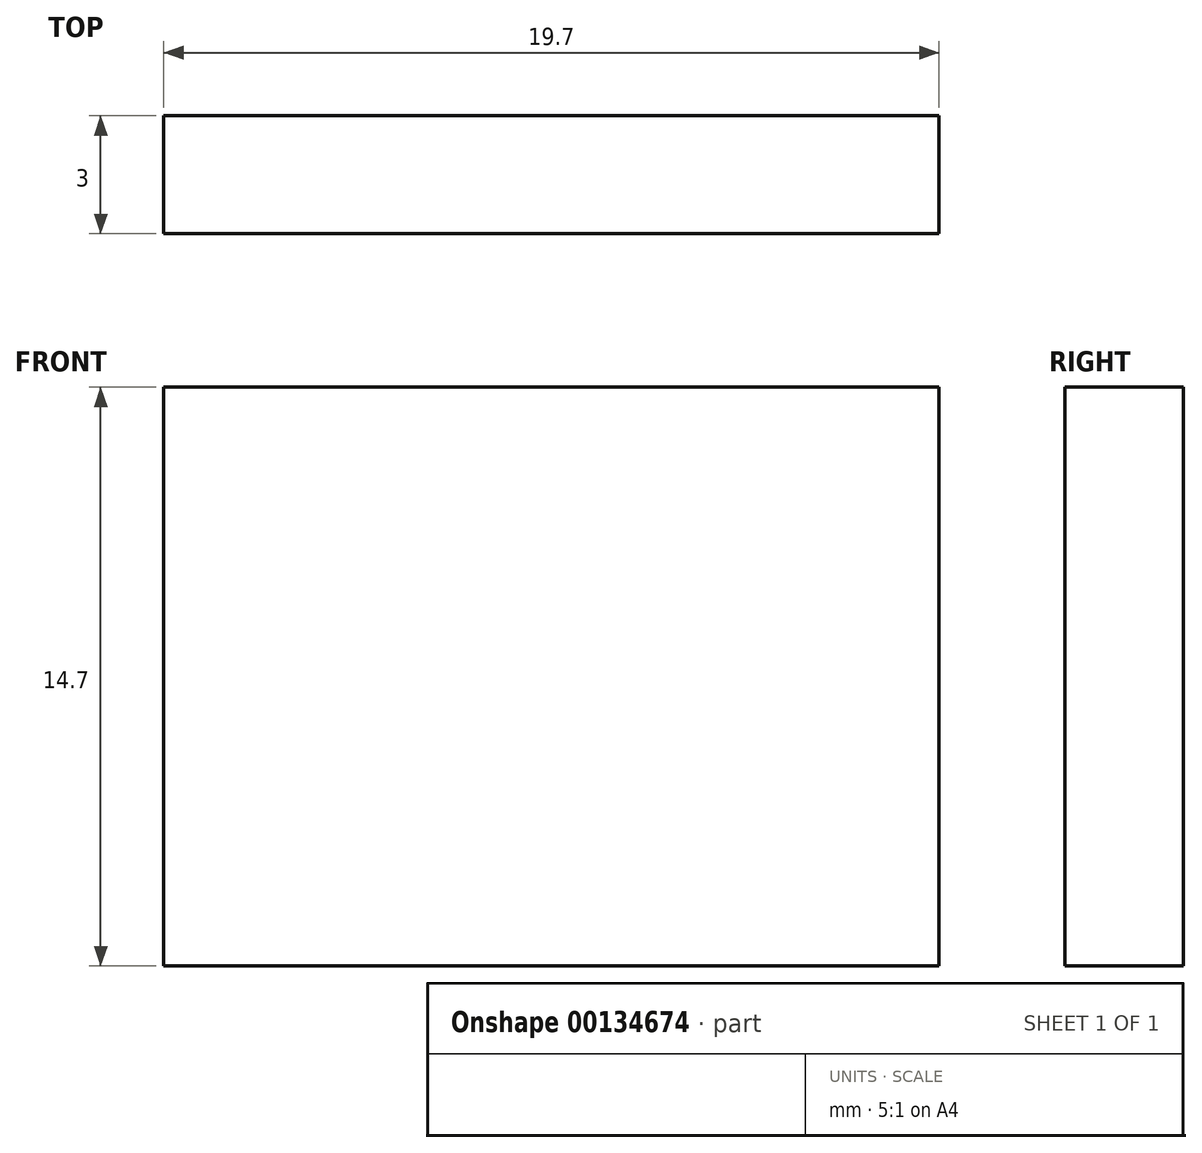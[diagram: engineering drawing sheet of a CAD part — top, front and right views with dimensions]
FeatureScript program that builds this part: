
annotation { "Feature Type Name" : "Feature", "Feature Type Description" : "" }
export const myFeature = defineFeature(function(context is Context, id is Id, definition is map)
    precondition{}
    {
        {
            assignVariable(context, id + "F0", {"name" : "speaker_add", "anyValue" : 1.7 * mm});
        }
        {
            assignVariable(context, id + "F1", {"name" : "speaker_width", "anyValue" : 18 * mm + getVariable(context, 'speaker_add')});
        }
        {
            var Q0;
            Q0=qCreatedBy(makeId("Right.planeOp"),FACE);
            var sketch = newSketch(context, id + "F2", { "sketchPlane" : qUnion([Q0])});
            skLineSegment(sketch, "E0.bottom", {"start": v(1.5, 7.35) * mm, "end": v(-1.5, 7.35) * mm});
            skLineSegment(sketch, "E0.top", {"start": v(1.5, -7.35) * mm, "end": v(-1.5, -7.35) * mm});
            skLineSegment(sketch, "E0.left", {"start": v(1.5, 7.35) * mm, "end": v(1.5, -7.35) * mm});
            skLineSegment(sketch, "E0.right", {"start": v(-1.5, 7.35) * mm, "end": v(-1.5, -7.35) * mm});
            skPoint(sketch, "E0.middle", {"position": v(0, 0) * mm});
            skSolve(sketch);
        }
        {
            var Q0;
            Q0=makeQuery(id+"F2.imprint","IMPRINT",FACE,{"disambiguationData":[TD([[makeQuery(id+"F2.imprint","IMPRINT",EDGE,{"derivedFrom":sQuery(id+"F2.wireOp",EDGE,"E0.bottom")}),1.0]])]});
            extrude(context, id + "F3", {"entities" : qUnion([Q0]), "depth" : getVariable(context, 'speaker_width')});
        }
    });
